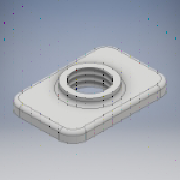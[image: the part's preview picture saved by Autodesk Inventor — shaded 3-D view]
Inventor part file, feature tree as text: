
AUTODESK INVENTOR PART (.ipt)
format: ipt  version: 2017 (Build 210142000, 142)  size: 177,152 bytes
history: native  units: mm
features: extrude x2, fillet x2, sketch x2, thread x1
ambient origin geometry x8: Origin, YZ Plane, XZ Plane, XY Plane, X Axis, Y Axis, Z Axis, Center Point
bodies: Solid1 (feature_tree)
feature tree (7):
  extrude  "Extrusion1"  Depth=15.0mm
  extrude  "Extrusion2"  Depth=2.0mm
  fillet  "Fillet1"  Radius=1.5mm
  thread  "Thread1"  [1 undecoded]
  fillet  "Fillet2"  Radius=1.0mm
  sketch  "Sketch1"  dims[d0=10.0mm d1=15.0mm]
  sketch  "Sketch2"  dims[d2=4.8mm d3=2.0mm d4=1.5mm d5=0.0mm d6=6.5mm d7=1.0mm d8=0.0mm d9=0.5mm d10=10.0mm d11=0.0mm d12=0.5mm]
note: 1 required parameter value undecoded (feature->parameter linkage not recoverable at this tier; creation-order binding heuristic only, values carry confidence <= 0.55)
